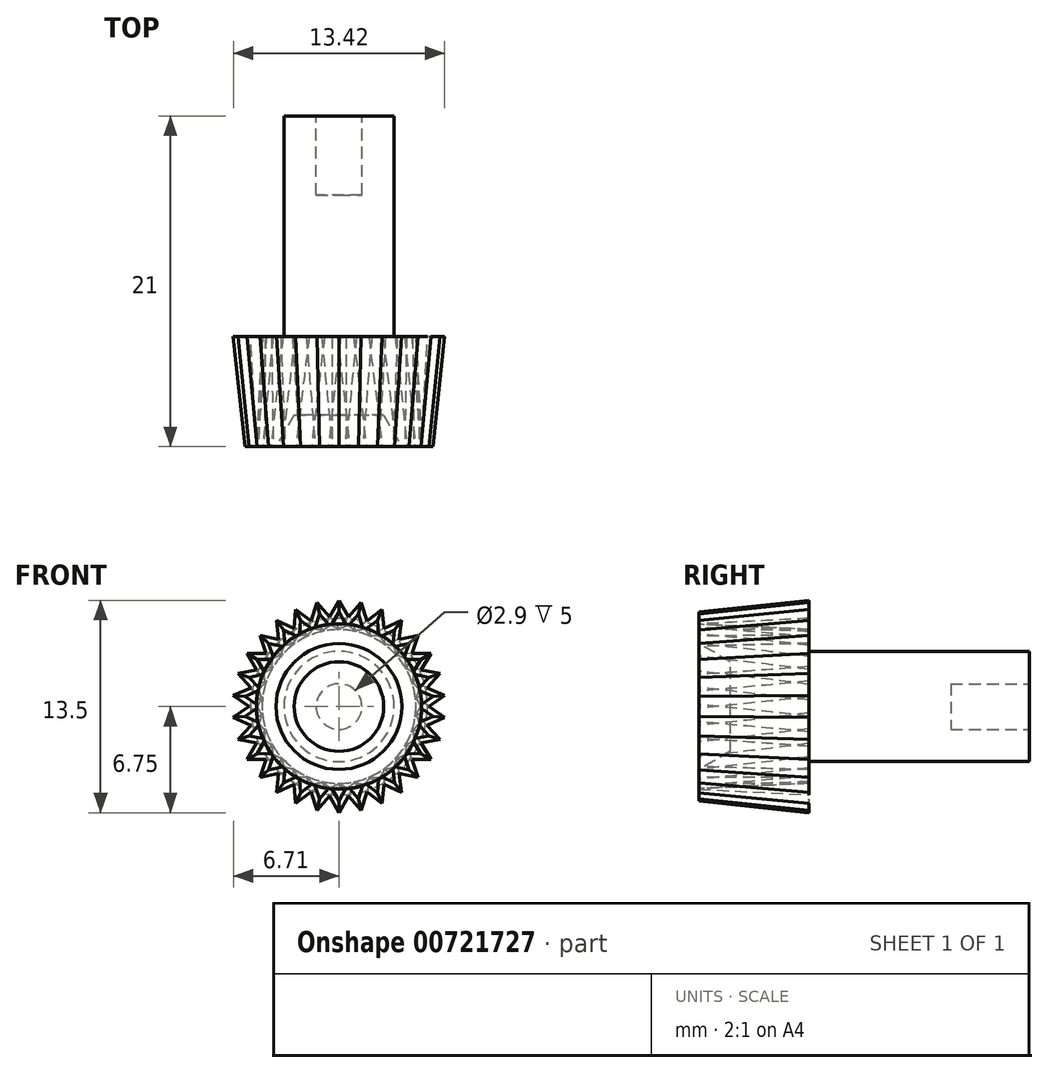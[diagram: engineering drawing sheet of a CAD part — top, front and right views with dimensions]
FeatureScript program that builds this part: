
annotation { "Feature Type Name" : "Feature", "Feature Type Description" : "" }
export const myFeature = defineFeature(function(context is Context, id is Id, definition is map)
    precondition{}
    {
        {
            var Q0;
            Q0=qCreatedBy(makeId("Front.planeOp"),FACE);
            var sketch = newSketch(context, id + "F0", { "sketchPlane" : qUnion([Q0])});
            skCircle(sketch, "E0", {"center": v(0, 0) * mm, "radius": 5.25 * mm});
            skLineSegment(sketch, "E1", {"start": v(0, 5.23) * mm, "end": v(0.43, 5.23) * mm});
            skLineSegment(sketch, "E2", {"start": v(0.43, 5.23) * mm, "end": v(0, 6) * mm});
            skLineSegment(sketch, "E3", {"start": v(0, 6) * mm, "end": v(-0.43, 5.23) * mm});
            skLineSegment(sketch, "E4", {"start": v(-0.43, 5.23) * mm, "end": v(0, 5.23) * mm});
            skSolve(sketch);
        }
        {
            var Q0;
            {var subQ0=sQuery(id+"F0.wireOp",EDGE,"E1");Q0=makeQuery(id+"F0.imprint","IMPRINT",FACE,{"disambiguationData":[TD([[makeQuery(id+"F0.imprint","IMPRINT",EDGE,{"derivedFrom":subQ0}),-1.0]])]});}
            var Q1;
            {var subQ0=sQuery(id+"F0.wireOp",EDGE,"E2");Q1=makeQuery(id+"F0.imprint","IMPRINT",FACE,{"disambiguationData":[TD([[makeQuery(id+"F0.imprint","IMPRINT",EDGE,{"derivedFrom":subQ0}),1.0]])]});}
            extrude(context, id + "F1", {"entities" : qUnion([Q0, Q1]), "oppositeDirection" : true, "depth" : 7 * mm, "offsetDistance" : 25 * mm, "hasDraft" : true, "draftAngle" : 3 * degree});
        }
        {
            var Q0;
            Q0=makeQuery(id+"F1.opExtrude","SWEPT_BODY",BODY,{"disambiguationData":[OSD([sQuery(id+"F0.wireOp",EDGE,"E0"),sQuery(id+"F0.wireOp",EDGE,"E2"),sQuery(id+"F0.wireOp",EDGE,"E3")])]});
            var Q1;
            {var subQ0=sQuery(id+"F0.wireOp",EDGE,"E0");Q1=makeQuery(id+"F1.opExtrude","SWEPT_FACE",FACE,{"disambiguationData":[OSD([subQ0]),TDD([makeQuery(id+"F0.imprint","IMPRINT",EDGE,{"disambiguationData":[TD([[makeQuery(id+"F0.imprint","INTERSECT",VERTEX,{"derivedFrom":[subQ0,sQuery(id+"F0.wireOp",EDGE,"E1"),sQuery(id+"F0.wireOp",EDGE,"E2")]}),1.0]])],"derivedFrom":subQ0})])]});}
            circularPattern(context, id + "F2", {"entities" : qUnion([Q0]), "axis" : qUnion([Q1]), "angle" : 360 * degree, "instanceCount" : 30, "equalSpace" : true});
        }
        {
            var Q0;
            Q0=makeQuery(id+"F1.opExtrude","CAP_FACE",FACE,{"disambiguationData":[OSD([sQuery(id+"F0.wireOp",EDGE,"E0"),sQuery(id+"F0.wireOp",EDGE,"E1"),sQuery(id+"F0.wireOp",EDGE,"E4")])],"isStart":true});
            var sketch = newSketch(context, id + "F3", { "sketchPlane" : qUnion([Q0])});
            skCircle(sketch, "E5", {"center": v(0, 0) * mm, "radius": 4 * mm});
            skSolve(sketch);
        }
        {
            var Q0;
            Q0=makeQuery(id+"F3.imprint","IMPRINT",FACE,{"disambiguationData":[TD([[makeQuery(id+"F3.imprint","IMPRINT",EDGE,{"derivedFrom":sQuery(id+"F3.wireOp",EDGE,"E5")}),1.0]])]});
            extrude(context, id + "F4", {"entities" : qUnion([Q0]), "operationType" : NewBodyOperationType.REMOVE, "oppositeDirection" : true, "depth" : 2 * mm, "offsetDistance" : 25 * mm, "hasDraft" : true, "draftAngle" : 30 * degree, "draftPullDirection" : true});
        }
        {
            var Q0;
            Q0=makeQuery(id+"F1.opExtrude","CAP_FACE",FACE,{"disambiguationData":[OSD([sQuery(id+"F0.wireOp",EDGE,"E0"),sQuery(id+"F0.wireOp",EDGE,"E1"),sQuery(id+"F0.wireOp",EDGE,"E4")])],"isStart":false});
            var sketch = newSketch(context, id + "F5", { "sketchPlane" : qUnion([Q0])});
            skCircle(sketch, "E6", {"center": v(0, 0) * mm, "radius": 3.5 * mm});
            skSolve(sketch);
        }
        {
            var Q0;
            Q0=makeQuery(id+"F5.imprint","IMPRINT",FACE,{"disambiguationData":[TD([[makeQuery(id+"F5.imprint","IMPRINT",EDGE,{"derivedFrom":sQuery(id+"F5.wireOp",EDGE,"E6")}),1.0]])]});
            extrude(context, id + "F6", {"entities" : qUnion([Q0]), "operationType" : NewBodyOperationType.ADD, "depth" : 14 * mm, "offsetDistance" : 25 * mm});
        }
        {
            var Q0;
            Q0=makeQuery(id+"F6.opExtrude","CAP_FACE",FACE,{"disambiguationData":[OSD([sQuery(id+"F5.wireOp",EDGE,"E6")])],"isStart":false});
            var sketch = newSketch(context, id + "F7", { "sketchPlane" : qUnion([Q0])});
            skCircle(sketch, "E7", {"center": v(0, 0) * mm, "radius": 1.45 * mm});
            skSolve(sketch);
        }
        {
            var Q0;
            Q0=makeQuery(id+"F7.imprint","IMPRINT",FACE,{"disambiguationData":[TD([[makeQuery(id+"F7.imprint","IMPRINT",EDGE,{"derivedFrom":sQuery(id+"F7.wireOp",EDGE,"E7")}),1.0]])]});
            extrude(context, id + "F8", {"entities" : qUnion([Q0]), "operationType" : NewBodyOperationType.REMOVE, "oppositeDirection" : true, "depth" : 5 * mm, "offsetDistance" : 25 * mm});
        }
    });
